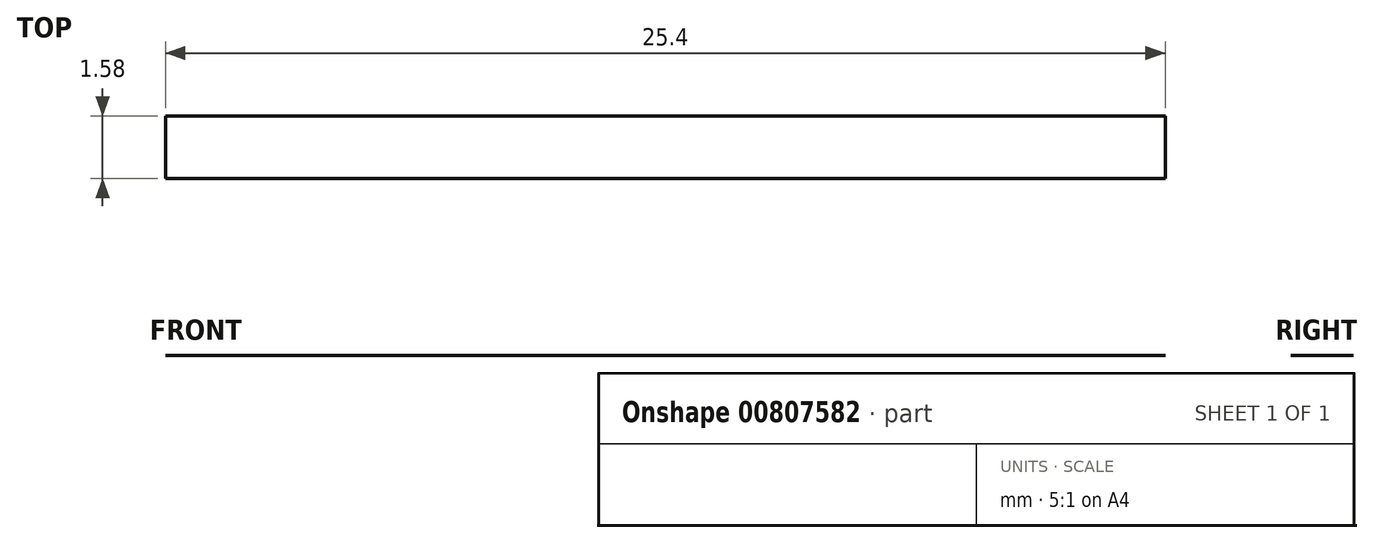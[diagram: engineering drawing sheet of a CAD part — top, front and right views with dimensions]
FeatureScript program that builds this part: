
annotation { "Feature Type Name" : "Feature", "Feature Type Description" : "" }
export const myFeature = defineFeature(function(context is Context, id is Id, definition is map)
    precondition{}
    {
        {
            var Q0;
            Q0=qCreatedBy(makeId("Top.planeOp"),FACE);
            var sketch = newSketch(context, id + "F0", { "sketchPlane" : qUnion([Q0])});
            skLineSegment(sketch, "E0.bottom", {"start": v(12.7, 0.8) * mm, "end": v(-12.7, 0.8) * mm});
            skLineSegment(sketch, "E0.top", {"start": v(12.7, -0.8) * mm, "end": v(-12.7, -0.8) * mm});
            skLineSegment(sketch, "E0.left", {"start": v(12.7, 0.8) * mm, "end": v(12.7, -0.8) * mm});
            skLineSegment(sketch, "E0.right", {"start": v(-12.7, 0.8) * mm, "end": v(-12.7, -0.8) * mm});
            skPoint(sketch, "E0.middle", {"position": v(0, 0) * mm});
            skSolve(sketch);
        }
        {
            var Q0;
            Q0 = qSketchRegion(id + "F0", true);
            extrude(context, id + "F1", {"entities" : qUnion([Q0]), "depth" : 1 / 203.2 * mm, "offsetDistance" : 25 * mm});
        }
    });
